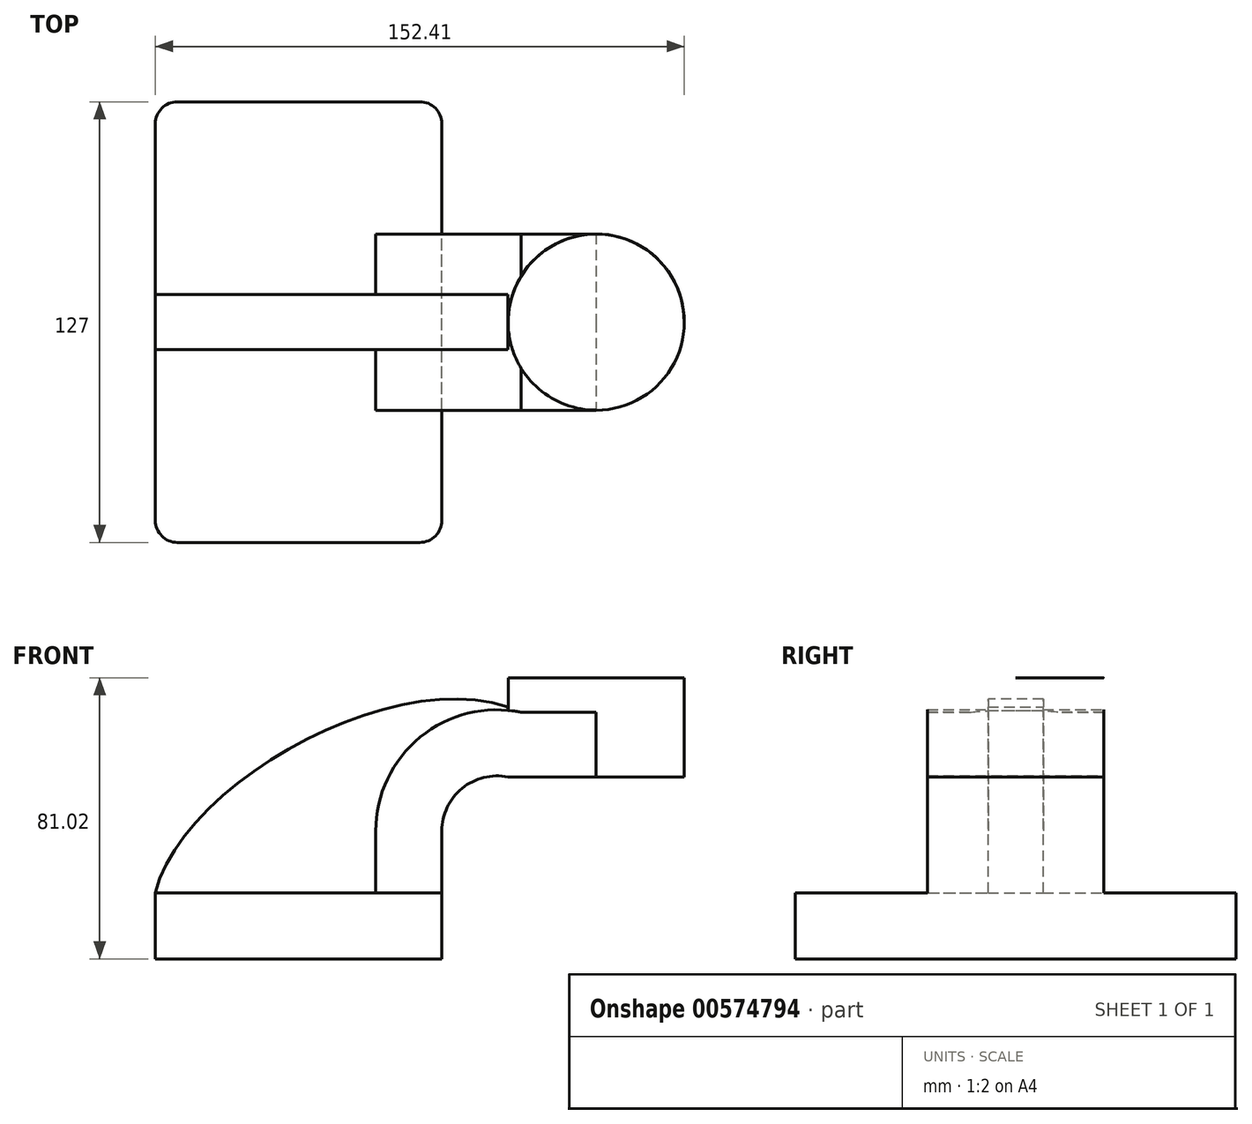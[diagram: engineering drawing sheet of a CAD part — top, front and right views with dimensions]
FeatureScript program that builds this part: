
annotation { "Feature Type Name" : "Feature", "Feature Type Description" : "" }
export const myFeature = defineFeature(function(context is Context, id is Id, definition is map)
    precondition{}
    {
        {
            var Q0;
            Q0=qCreatedBy(makeId("Right.planeOp"),FACE);
            var sketch = newSketch(context, id + "F0", { "sketchPlane" : qUnion([Q0])});
            skSolve(sketch);
        }
        {
            var Q0;
            Q0=qCreatedBy(makeId("Front.planeOp"),FACE);
            var sketch = newSketch(context, id + "F1", { "sketchPlane" : qUnion([Q0])});
            skLineSegment(sketch, "E0.bottom", {"start": v(41.28, -9.52) * mm, "end": v(-41.28, -9.52) * mm});
            skLineSegment(sketch, "E0.top", {"start": v(41.28, 9.53) * mm, "end": v(-41.28, 9.53) * mm});
            skLineSegment(sketch, "E0.left", {"start": v(41.28, -9.52) * mm, "end": v(41.28, 9.53) * mm});
            skLineSegment(sketch, "E0.right", {"start": v(-41.28, -9.52) * mm, "end": v(-41.28, 9.53) * mm});
            skPoint(sketch, "E0.middle", {"position": v(0, 0) * mm});
            skLineSegment(sketch, "E1.bottom", {"start": v(111.13, 42.88) * mm, "end": v(60.33, 42.88) * mm});
            skLineSegment(sketch, "E1.top", {"start": v(111.12, 71.45) * mm, "end": v(60.32, 71.45) * mm});
            skLineSegment(sketch, "E1.left", {"start": v(111.13, 42.88) * mm, "end": v(111.12, 71.45) * mm});
            skLineSegment(sketch, "E1.right", {"start": v(60.33, 42.88) * mm, "end": v(60.32, 71.45) * mm});
            skPoint(sketch, "E1.middle", {"position": v(85.72, 57.16) * mm});
            skLineSegment(sketch, "E2", {"start": v(41.28, 9.53) * mm, "end": v(41.28, 27.32) * mm});
            skArc(sketch, "E3", {"start": v(41.27, 27.32) * mm, "mid": v(47.1, 39.62) * mm, "end": v(60.33, 42.88) * mm});
            skArc(sketch, "E4.0", {"start": v(22.23, 27.32) * mm, "mid": v(35.06, 54.37) * mm, "end": v(64.13, 61.54) * mm});
            skLineSegment(sketch, "E4.1", {"start": v(22.22, 9.53) * mm, "end": v(22.22, 27.32) * mm});
            skLineSegment(sketch, "E5", {"start": v(64.13, 61.54) * mm, "end": v(74.94, 61.54) * mm});
            skLineSegment(sketch, "E6", {"start": v(74.94, 61.54) * mm, "end": v(85.75, 61.54) * mm});
            skLineSegment(sketch, "E7", {"start": v(85.75, 61.54) * mm, "end": v(85.72, 57.16) * mm});
            skLineSegment(sketch, "E8", {"start": v(85.72, 42.88) * mm, "end": v(85.75, 71.45) * mm});
            skFitSpline(sketch, "E9", {"points": [v(-41.28, 9.52) * mm, v(64.13, 61.54) * mm], "startDerivative": vector(24.28, 97.8) * mm, "endDerivative": vector(99.57, -46.9) * mm});
            skSolve(sketch);
        }
        {
            var Q0;
            Q0=makeQuery(id+"F1.imprint","IMPRINT",FACE,{"disambiguationData":[TD([[makeQuery(id+"F1.imprint","IMPRINT",EDGE,{"derivedFrom":sQuery(id+"F1.wireOp",EDGE,"E0.bottom")}),-1.0]])]});
            extrude(context, id + "F2", {"entities" : qUnion([Q0]), "endBound" : BoundingType.SYMMETRIC, "depth" : 127 * mm, "offsetDistance" : 25.4 * mm});
        }
        {
            var Q0;
            Q0 = qSketchRegion(id + "F0", true);
            var Q1;
            {var subQ4=sQuery(id+"F1.wireOp",EDGE,"E2");Q1=makeQuery(id+"F1.imprint","IMPRINT",FACE,{"disambiguationData":[TD([[makeQuery(id+"F1.imprint","IMPRINT",EDGE,{"derivedFrom":subQ4}),1.0]])]});}
            var Q2;
            {var subQ5=sQuery(id+"F1.wireOp",EDGE,"E5");Q2=makeQuery(id+"F1.imprint","IMPRINT",FACE,{"disambiguationData":[TD([[makeQuery(id+"F1.imprint","IMPRINT",EDGE,{"derivedFrom":subQ5}),-1.0]])]});}
            extrude(context, id + "F3", {"entities" : qUnion([Q0, Q1, Q2]), "operationType" : NewBodyOperationType.ADD, "endBound" : BoundingType.SYMMETRIC, "depth" : 50.8 * mm, "offsetDistance" : 25.4 * mm});
        }
        {
            var Q0;
            {var subQ5=sQuery(id+"F1.wireOp",EDGE,"E4.1");Q0=makeQuery(id+"F1.imprint","IMPRINT",FACE,{"disambiguationData":[TD([[makeQuery(id+"F1.imprint","IMPRINT",EDGE,{"derivedFrom":subQ5}),1.0]])]});}
            extrude(context, id + "F4", {"entities" : qUnion([Q0]), "operationType" : NewBodyOperationType.ADD, "endBound" : BoundingType.SYMMETRIC, "depth" : 15.88 * mm, "offsetDistance" : 25.4 * mm});
        }
        {
            var Q0;
            {var subQ0=sQuery(id+"F1.wireOp",EDGE,"E1.left");Q0=makeQuery(id+"F1.imprint","IMPRINT",FACE,{"disambiguationData":[TD([[makeQuery(id+"F1.imprint","IMPRINT",EDGE,{"derivedFrom":subQ0}),1.0]])]});}
            var Q1;
            Q1=sQuery(id+"F1.wireOp",EDGE,"E8");
            revolve(context, id + "F5", {"operationType" : NewBodyOperationType.ADD, "entities" : qUnion([Q0]), "axis" : qUnion([Q1]), "revolveType" : RevolveType.FULL});
        }
        {
            var Q0;
            Q0=makeQuery(id+"F2.opExtrude","CAP_EDGE",EDGE,{"disambiguationData":[OSD([sQuery(id+"F1.wireOp",EDGE,"E0.right")])],"isStart":false});
            var Q1;
            Q1=makeQuery(id+"F2.opExtrude","CAP_EDGE",EDGE,{"disambiguationData":[OSD([sQuery(id+"F1.wireOp",EDGE,"E0.left")])],"isStart":false});
            var Q2;
            Q2=makeQuery(id+"F2.opExtrude","CAP_EDGE",EDGE,{"disambiguationData":[OSD([sQuery(id+"F1.wireOp",EDGE,"E0.left")])],"isStart":true});
            var Q3;
            Q3=makeQuery(id+"F2.opExtrude","CAP_EDGE",EDGE,{"disambiguationData":[OSD([sQuery(id+"F1.wireOp",EDGE,"E0.right")])],"isStart":true});
            fillet(context, id + "F6", {"entities" : qUnion([Q0, Q1, Q2, Q3]), "radius" : 6.35 * mm, "tangentPropagation" : true, "allowEdgeOverflow" : false});
        }
    });
